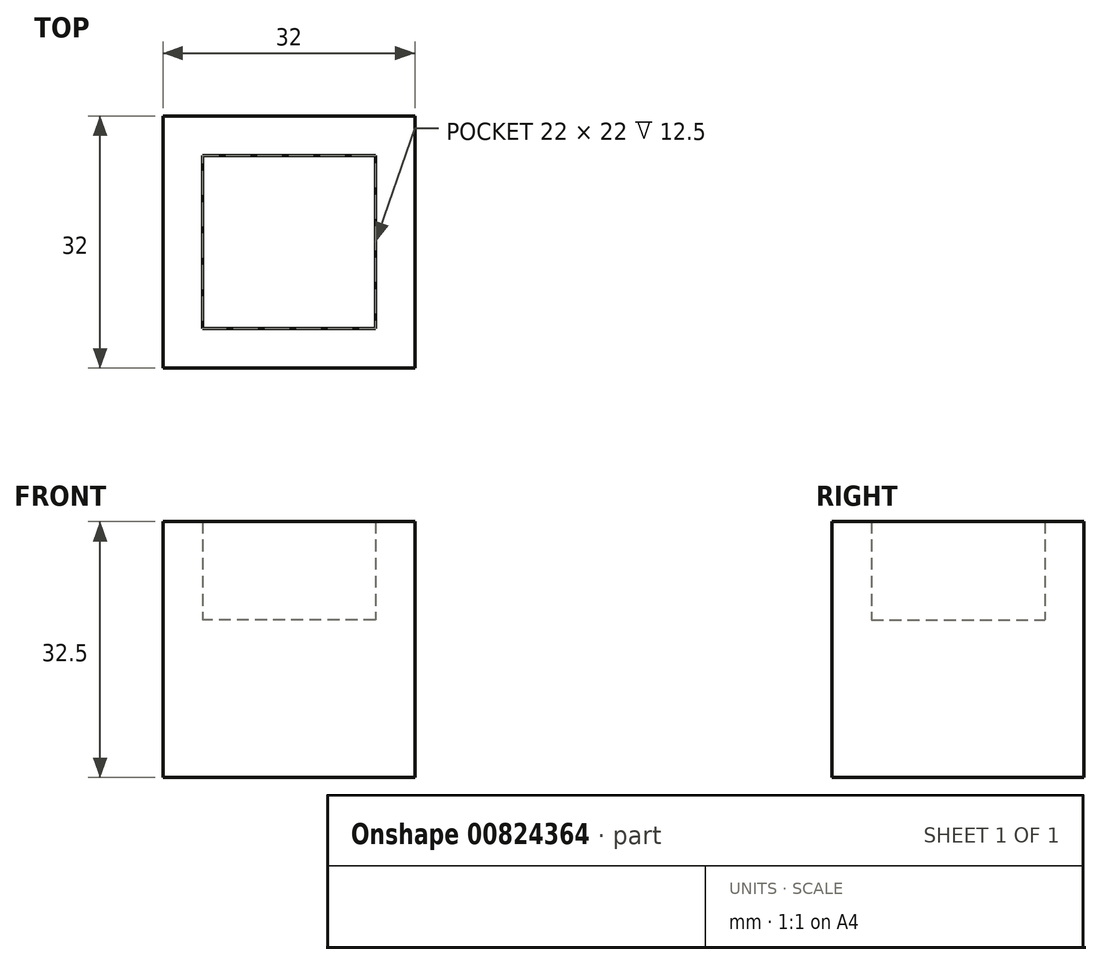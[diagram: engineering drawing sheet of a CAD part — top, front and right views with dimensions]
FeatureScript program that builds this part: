
annotation { "Feature Type Name" : "Feature", "Feature Type Description" : "" }
export const myFeature = defineFeature(function(context is Context, id is Id, definition is map)
    precondition{}
    {
        {
            var Q0;
            Q0=qCreatedBy(makeId("Top.planeOp"),FACE);
            var sketch = newSketch(context, id + "F0", { "sketchPlane" : qUnion([Q0])});
            skLineSegment(sketch, "E0.bottom", {"start": v(11, -11) * mm, "end": v(-11, -11) * mm});
            skLineSegment(sketch, "E0.top", {"start": v(11, 11) * mm, "end": v(-11, 11) * mm});
            skLineSegment(sketch, "E0.left", {"start": v(11, -11) * mm, "end": v(11, 11) * mm});
            skLineSegment(sketch, "E0.right", {"start": v(-11, -11) * mm, "end": v(-11, 11) * mm});
            skPoint(sketch, "E0.middle", {"position": v(0, 0) * mm});
            skLineSegment(sketch, "E1.0", {"start": v(-16, -16) * mm, "end": v(-16, 16) * mm});
            skLineSegment(sketch, "E1.1", {"start": v(16, -16) * mm, "end": v(-16, -16) * mm});
            skLineSegment(sketch, "E1.2", {"start": v(16, -16) * mm, "end": v(16, 16) * mm});
            skLineSegment(sketch, "E1.3", {"start": v(16, 16) * mm, "end": v(-16, 16) * mm});
            skSolve(sketch);
        }
        {
            var Q0;
            Q0=makeQuery(id+"F0.imprint","IMPRINT",FACE,{"disambiguationData":[TD([[makeQuery(id+"F0.imprint","IMPRINT",EDGE,{"derivedFrom":sQuery(id+"F0.wireOp",EDGE,"E0.bottom")}),1.0]])]});
            extrude(context, id + "F1", {"entities" : qUnion([Q0]), "depth" : 12.5 * mm, "offsetDistance" : 25 * mm});
        }
        {
            var Q0;
            Q0=makeQuery(id+"F0.imprint","IMPRINT",FACE,{"disambiguationData":[TD([[makeQuery(id+"F0.imprint","IMPRINT",EDGE,{"derivedFrom":sQuery(id+"F0.wireOp",EDGE,"E0.bottom")}),-1.0]])]});
            var Q1;
            Q1=makeQuery(id+"F0.imprint","IMPRINT",FACE,{"disambiguationData":[TD([[makeQuery(id+"F0.imprint","IMPRINT",EDGE,{"derivedFrom":sQuery(id+"F0.wireOp",EDGE,"E0.bottom")}),1.0]])]});
            extrude(context, id + "F2", {"entities" : qUnion([Q0, Q1]), "operationType" : NewBodyOperationType.ADD, "oppositeDirection" : true, "depth" : 20 * mm, "offsetDistance" : 25 * mm});
        }
    });
